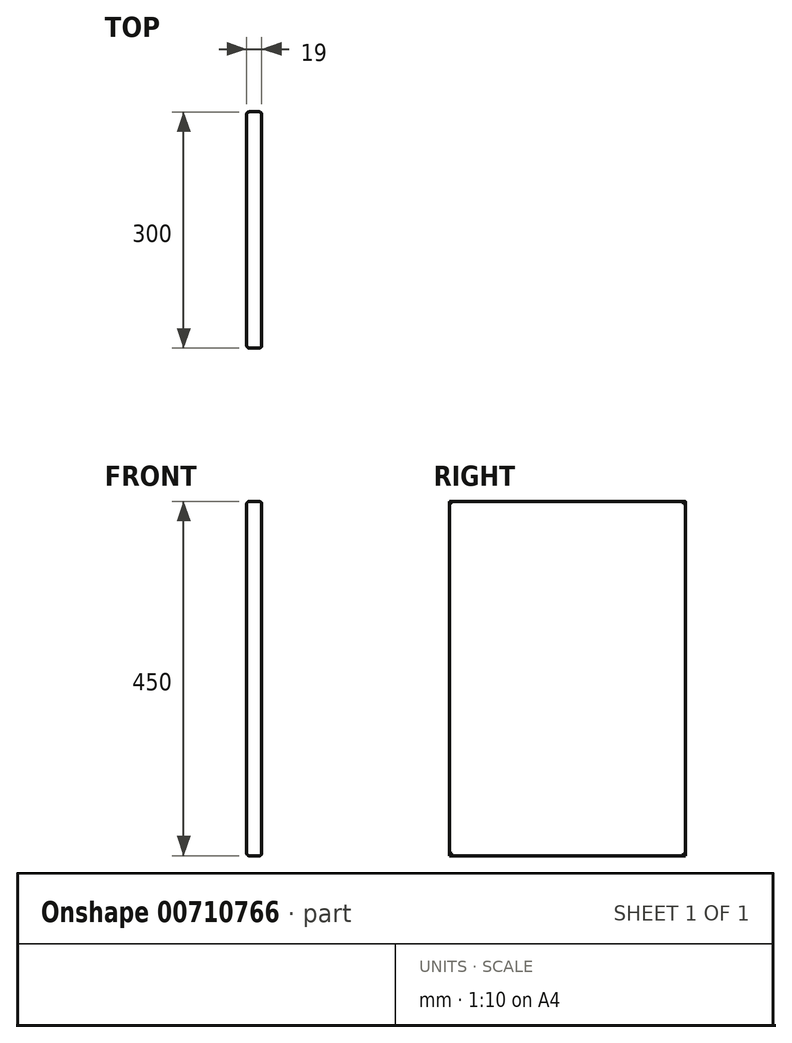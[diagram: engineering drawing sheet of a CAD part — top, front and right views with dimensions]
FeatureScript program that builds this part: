
annotation { "Feature Type Name" : "Feature", "Feature Type Description" : "" }
export const myFeature = defineFeature(function(context is Context, id is Id, definition is map)
    precondition{}
    {
        {
            var Q0;
            Q0=qCreatedBy(makeId("Right.planeOp"),FACE);
            var sketch = newSketch(context, id + "F0", { "sketchPlane" : qUnion([Q0])});
            skLineSegment(sketch, "E0.bottom", {"start": v(-183.88, 267.33) * mm, "end": v(116.12, 267.33) * mm});
            skLineSegment(sketch, "E0.top", {"start": v(-183.88, -182.67) * mm, "end": v(116.12, -182.67) * mm});
            skLineSegment(sketch, "E0.left", {"start": v(-183.88, 267.33) * mm, "end": v(-183.88, -182.67) * mm});
            skLineSegment(sketch, "E0.right", {"start": v(116.12, 267.33) * mm, "end": v(116.12, -182.67) * mm});
            skSolve(sketch);
        }
        {
            var Q0;
            Q0=makeQuery(id+"F0.imprint","IMPRINT",FACE,{"disambiguationData":[TD([[makeQuery(id+"F0.imprint","IMPRINT",EDGE,{"derivedFrom":sQuery(id+"F0.wireOp",EDGE,"E0.bottom")}),-1.0]])]});
            extrude(context, id + "F1", {"entities" : qUnion([Q0]), "depth" : 19 * mm, "offsetDistance" : 25 * mm});
        }
        {
            var Q0;
            Q0=makeQuery(id+"F1.opExtrude","CAP_EDGE",EDGE,{"disambiguationData":[OSD([sQuery(id+"F0.wireOp",EDGE,"E0.left")])],"isStart":false});
            var Q1;
            Q1=makeQuery(id+"F1.opExtrude","CAP_EDGE",EDGE,{"disambiguationData":[OSD([sQuery(id+"F0.wireOp",EDGE,"E0.bottom")])],"isStart":false});
            var Q2;
            Q2=makeQuery(id+"F1.opExtrude","CAP_EDGE",EDGE,{"disambiguationData":[OSD([sQuery(id+"F0.wireOp",EDGE,"E0.right")])],"isStart":false});
            var Q3;
            Q3=makeQuery(id+"F1.opExtrude","CAP_EDGE",EDGE,{"disambiguationData":[OSD([sQuery(id+"F0.wireOp",EDGE,"E0.top")])],"isStart":false});
            var Q4;
            Q4=makeQuery(id+"F1.opExtrude","CAP_EDGE",EDGE,{"disambiguationData":[OSD([sQuery(id+"F0.wireOp",EDGE,"E0.left")])],"isStart":true});
            var Q5;
            Q5=makeQuery(id+"F1.opExtrude","CAP_EDGE",EDGE,{"disambiguationData":[OSD([sQuery(id+"F0.wireOp",EDGE,"E0.right")])],"isStart":true});
            var Q6;
            Q6=makeQuery(id+"F1.opExtrude","CAP_EDGE",EDGE,{"disambiguationData":[OSD([sQuery(id+"F0.wireOp",EDGE,"E0.top")])],"isStart":true});
            var Q7;
            Q7=makeQuery(id+"F1.opExtrude","CAP_EDGE",EDGE,{"disambiguationData":[OSD([sQuery(id+"F0.wireOp",EDGE,"E0.bottom")])],"isStart":true});
            fillet(context, id + "F2", {"entities" : qUnion([Q0, Q1, Q2, Q3, Q4, Q5, Q6, Q7]), "radius" : 3 * mm, "tangentPropagation" : true, "allowEdgeOverflow" : false});
        }
    });
